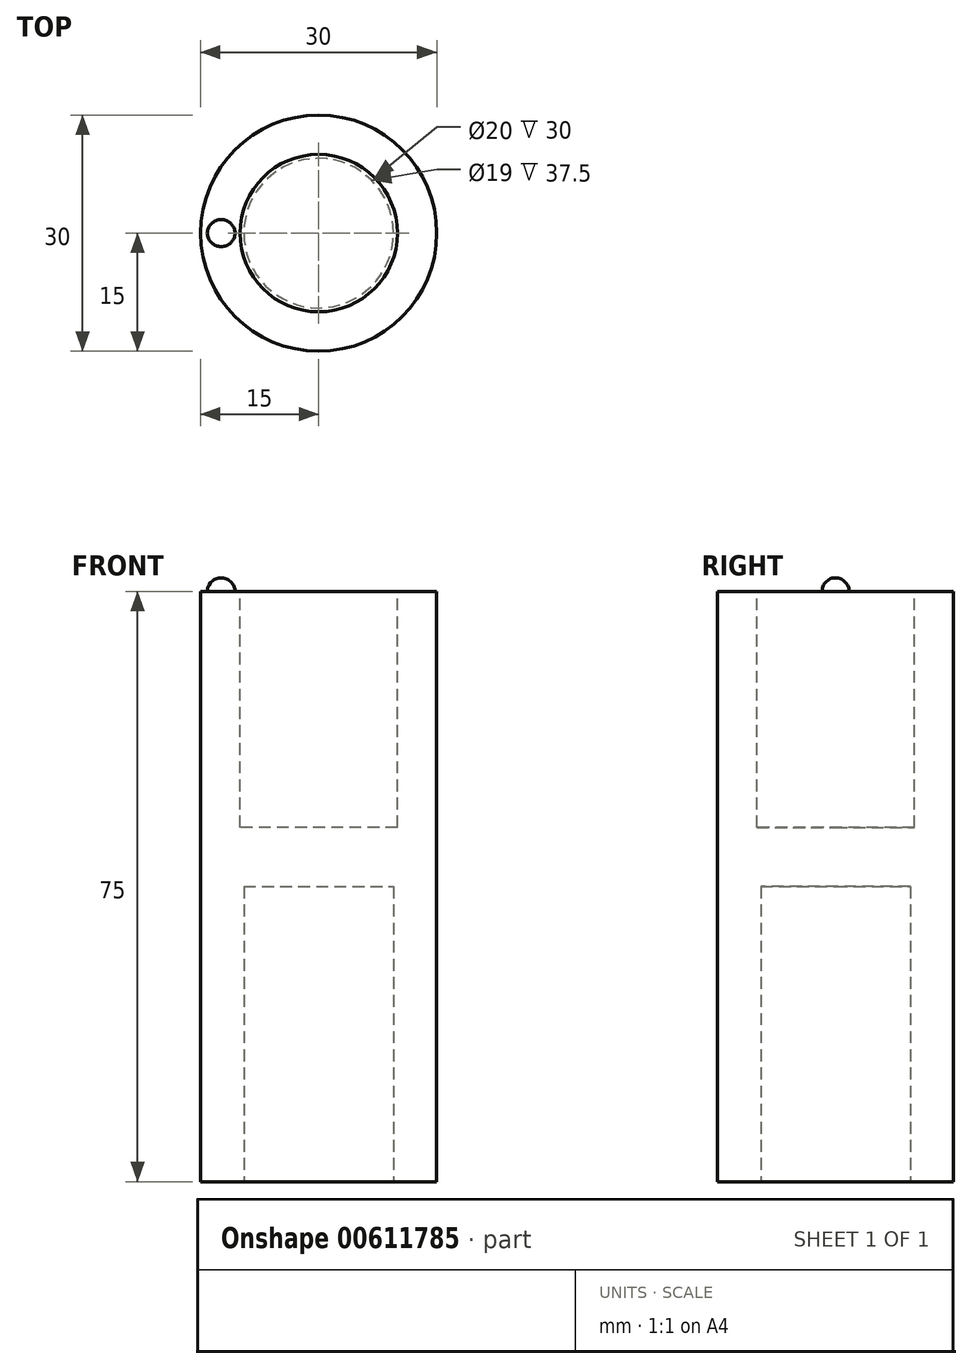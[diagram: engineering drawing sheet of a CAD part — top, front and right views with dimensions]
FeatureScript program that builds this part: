
annotation { "Feature Type Name" : "Feature", "Feature Type Description" : "" }
export const myFeature = defineFeature(function(context is Context, id is Id, definition is map)
    precondition{}
    {
        {
            var Q0;
            Q0=qCreatedBy(makeId("Top.planeOp"),FACE);
            var sketch = newSketch(context, id + "F0", { "sketchPlane" : qUnion([Q0])});
            skCircle(sketch, "E0", {"center": v(0, 0) * mm, "radius": 15 * mm});
            skSolve(sketch);
        }
        {
            var Q0;
            Q0=makeQuery(id+"F0.imprint","IMPRINT",FACE,{"disambiguationData":[TD([[makeQuery(id+"F0.imprint","IMPRINT",EDGE,{"derivedFrom":sQuery(id+"F0.wireOp",EDGE,"E0")}),1.0]])]});
            extrude(context, id + "F1", {"entities" : qUnion([Q0]), "depth" : 75 * mm, "offsetDistance" : 25 * mm});
        }
        {
            var Q0;
            Q0=makeQuery(id+"F1.opExtrude","CAP_FACE",FACE,{"disambiguationData":[OSD([sQuery(id+"F0.wireOp",EDGE,"E0")])],"isStart":false});
            var sketch = newSketch(context, id + "F2", { "sketchPlane" : qUnion([Q0])});
            skCircle(sketch, "E1", {"center": v(0, 0) * mm, "radius": 10 * mm});
            skSolve(sketch);
        }
        {
            var Q0;
            Q0=makeQuery(id+"F2.imprint","IMPRINT",FACE,{"disambiguationData":[TD([[makeQuery(id+"F2.imprint","IMPRINT",EDGE,{"derivedFrom":sQuery(id+"F2.wireOp",EDGE,"E1")}),1.0]])]});
            extrude(context, id + "F3", {"entities" : qUnion([Q0]), "operationType" : NewBodyOperationType.REMOVE, "oppositeDirection" : true, "depth" : 30 * mm, "offsetDistance" : 25 * mm});
        }
        {
            var Q0;
            Q0=makeQuery(id+"F1.opExtrude","CAP_FACE",FACE,{"disambiguationData":[OSD([sQuery(id+"F0.wireOp",EDGE,"E0")])],"isStart":false});
            var sketch = newSketch(context, id + "F4", { "sketchPlane" : qUnion([Q0])});
            skLineSegment(sketch, "E2", {"start": v(-10.62, 0) * mm, "end": v(-14.15, 0) * mm});
            skArc(sketch, "E3", {"start": v(-10.62, 0) * mm, "mid": v(-12.39, 1.71) * mm, "end": v(-14.15, 0) * mm});
            skSolve(sketch);
        }
        {
            var Q0;
            Q0=makeQuery(id+"F4.imprint","IMPRINT",FACE,{"disambiguationData":[TD([[makeQuery(id+"F4.imprint","IMPRINT",EDGE,{"derivedFrom":sQuery(id+"F4.wireOp",EDGE,"E2")}),-1.0]])]});
            var Q1;
            Q1=sQuery(id+"F4.wireOp",EDGE,"E2");
            revolve(context, id + "F5", {"operationType" : NewBodyOperationType.ADD, "entities" : qUnion([Q0]), "axis" : qUnion([Q1]), "revolveType" : RevolveType.TWO_DIRECTIONS, "angle" : 180 * degree, "angleBack" : 180 * degree});
        }
        {
            var Q0;
            Q0=makeQuery(id+"F1.opExtrude","CAP_FACE",FACE,{"disambiguationData":[OSD([sQuery(id+"F0.wireOp",EDGE,"E0")])],"isStart":true});
            var sketch = newSketch(context, id + "F6", { "sketchPlane" : qUnion([Q0])});
            skCircle(sketch, "E4", {"center": v(0, 0) * mm, "radius": 9.5 * mm});
            skSolve(sketch);
        }
        {
            var Q0;
            Q0=makeQuery(id+"F6.imprint","IMPRINT",FACE,{"disambiguationData":[TD([[makeQuery(id+"F6.imprint","IMPRINT",EDGE,{"derivedFrom":sQuery(id+"F6.wireOp",EDGE,"E4")}),1.0]])]});
            extrude(context, id + "F7", {"entities" : qUnion([Q0]), "operationType" : NewBodyOperationType.REMOVE, "oppositeDirection" : true, "depth" : 37.5 * mm, "offsetDistance" : 25 * mm});
        }
    });
